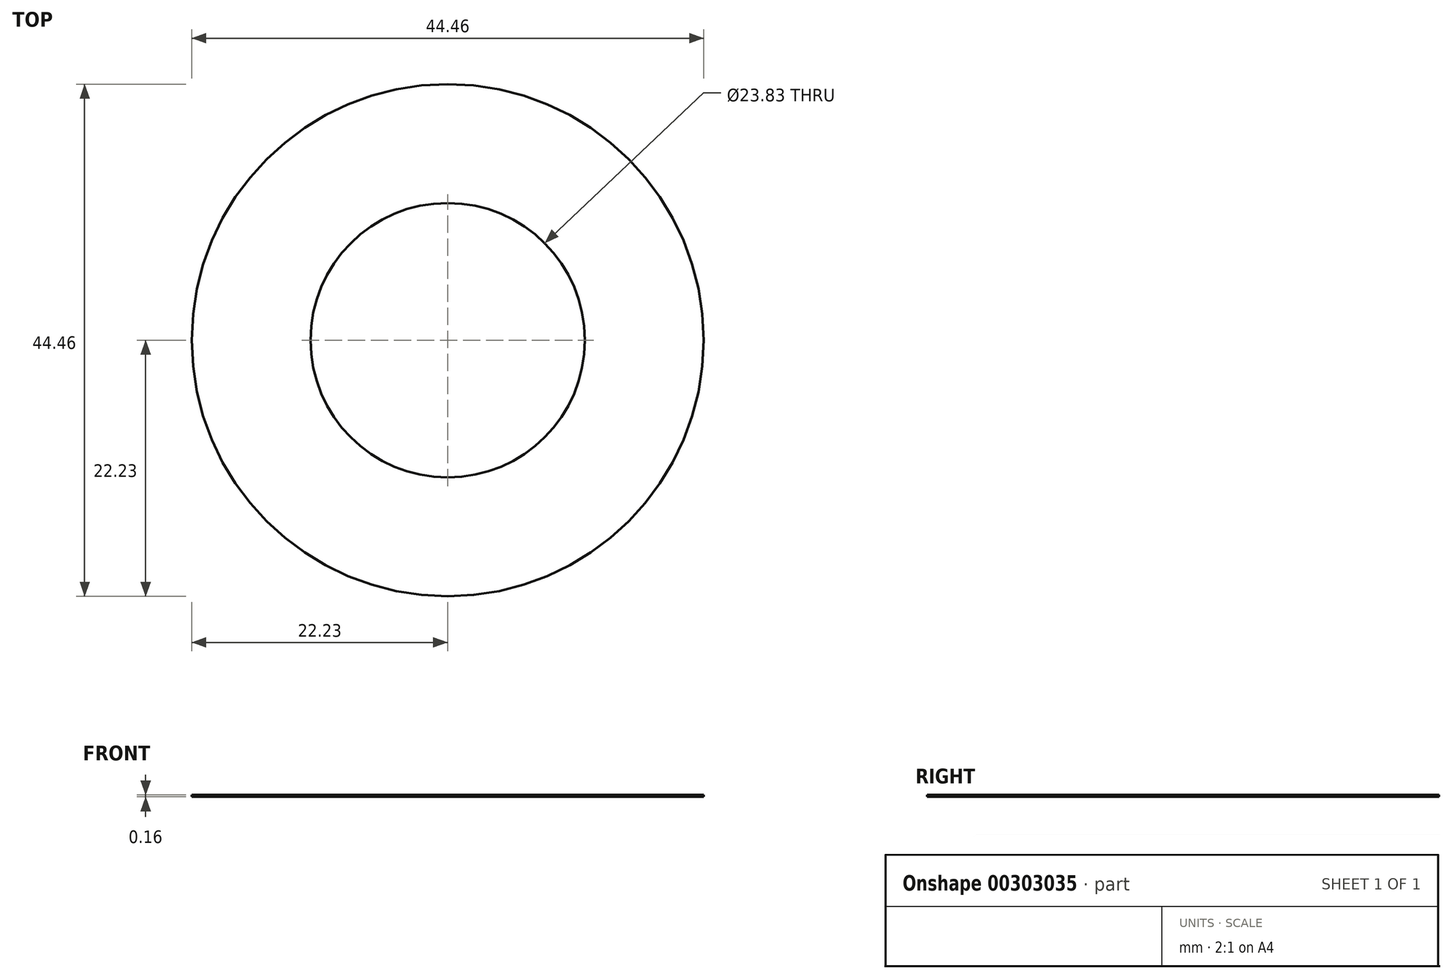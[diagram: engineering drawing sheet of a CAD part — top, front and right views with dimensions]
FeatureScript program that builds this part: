
annotation { "Feature Type Name" : "Feature", "Feature Type Description" : "" }
export const myFeature = defineFeature(function(context is Context, id is Id, definition is map)
    precondition{}
    {
        {
            var Q0;
            Q0=qCreatedBy(makeId("Top.planeOp"),FACE);
            var sketch = newSketch(context, id + "F0", { "sketchPlane" : qUnion([Q0])});
            skCircle(sketch, "E0", {"center": v(0, 0) * mm, "radius": 11.91 * mm});
            skCircle(sketch, "E1", {"center": v(0, 0) * mm, "radius": 22.23 * mm});
            skSolve(sketch);
        }
        {
            var Q0;
            Q0=makeQuery(id+"F0.imprint","IMPRINT",FACE,{"disambiguationData":[TD([[makeQuery(id+"F0.imprint","IMPRINT",EDGE,{"derivedFrom":sQuery(id+"F0.wireOp",EDGE,"E0")}),-1.0]])]});
            extrude(context, id + "F1", {"entities" : qUnion([Q0]), "depth" : ((.136 + .177) / 2) * mm, "symmetric" : true});
        }
    });
